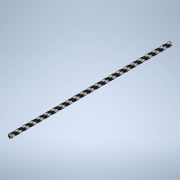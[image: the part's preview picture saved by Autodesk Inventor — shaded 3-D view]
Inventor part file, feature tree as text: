
AUTODESK INVENTOR PART (.ipt)
format: ipt  version: 2020 (Build 240168000, 168)  size: 102,400 bytes
history: native  units: in
note: dims shown in document units (in); Inventor stores cm internally (conversion verified against a paired STEP export)
features: extrude x1, sketch x1
ambient origin geometry x8: Origin, YZ Plane, XZ Plane, XY Plane, X Axis, Y Axis, Z Axis, Center Point
bodies: Solid1 (feature_tree)
feature tree (2):
  extrude  "Extrusion1"  Depth=3.2705in
  sketch  "Sketch1"  dims[d0=0.0787in d1=3.2705in d2=0.0in]
